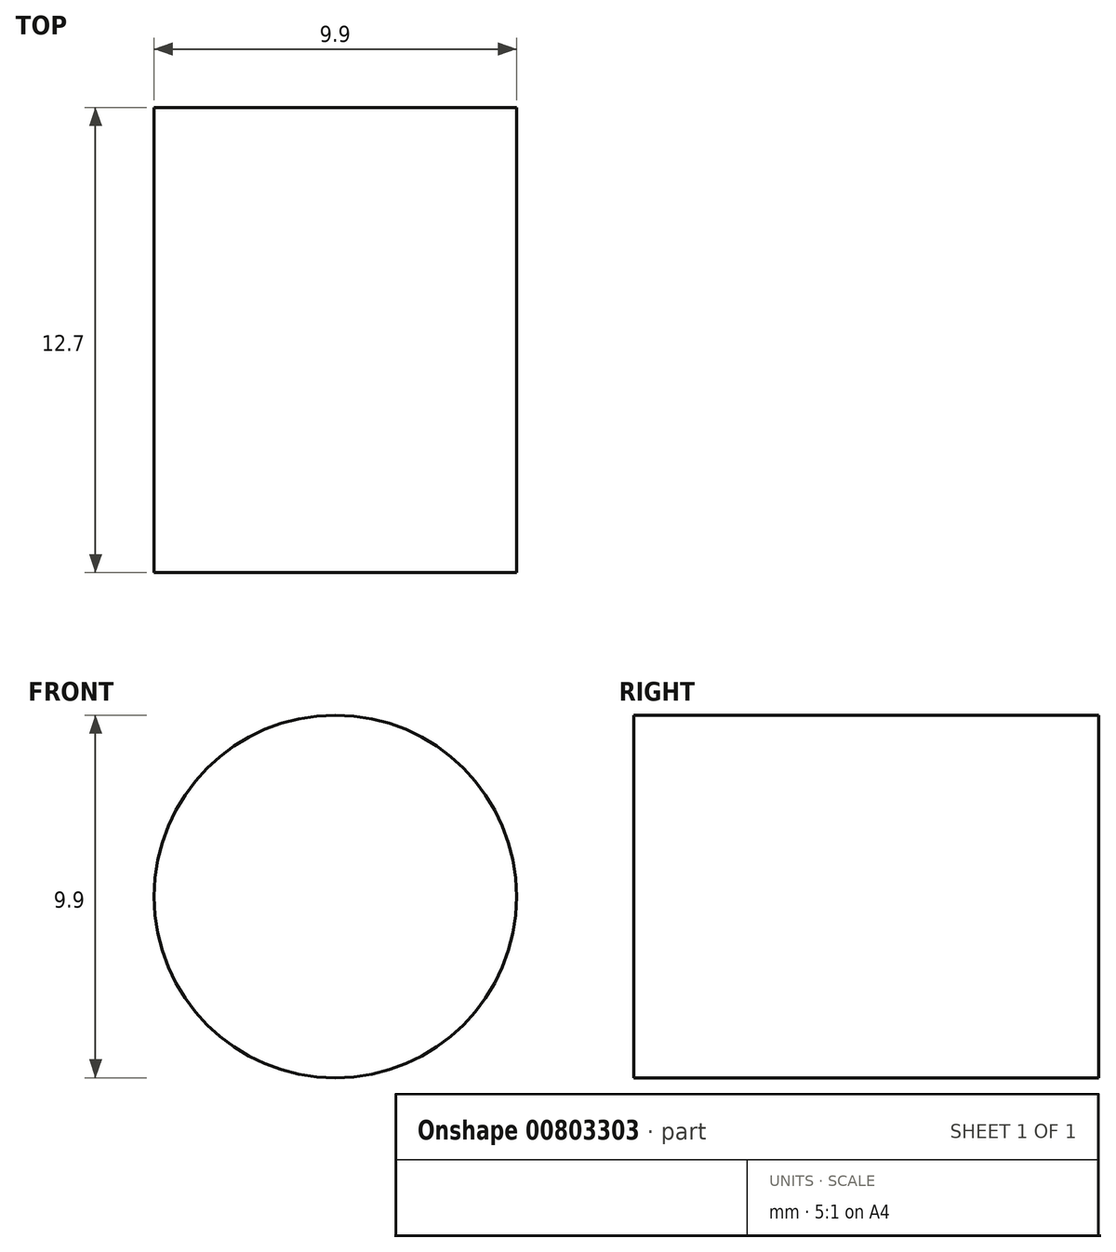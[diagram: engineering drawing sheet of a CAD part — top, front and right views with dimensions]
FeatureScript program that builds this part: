
annotation { "Feature Type Name" : "Feature", "Feature Type Description" : "" }
export const myFeature = defineFeature(function(context is Context, id is Id, definition is map)
    precondition{}
    {
        {
            var Q0;
            Q0=qCreatedBy(makeId("Front.planeOp"),FACE);
            var sketch = newSketch(context, id + "F0", { "sketchPlane" : qUnion([Q0])});
            skCircle(sketch, "E0", {"center": v(0, 0) * mm, "radius": 4.95 * mm});
            skSolve(sketch);
        }
        {
            var Q0;
            Q0=makeQuery(id+"F0.imprint","IMPRINT",FACE,{"disambiguationData":[TD([[makeQuery(id+"F0.imprint","IMPRINT",EDGE,{"derivedFrom":sQuery(id+"F0.wireOp",EDGE,"E0")}),1.0]])]});
            extrude(context, id + "F1", {"entities" : qUnion([Q0]), "depth" : 12.7 * mm, "offsetDistance" : 25.4 * mm});
        }
    });
